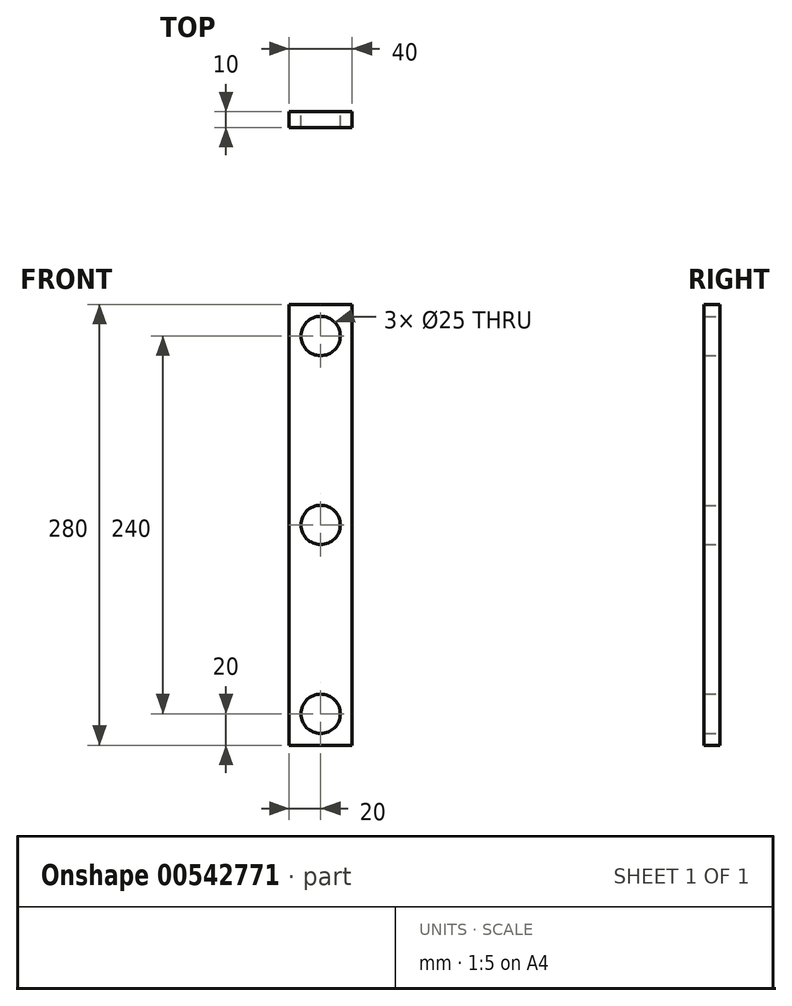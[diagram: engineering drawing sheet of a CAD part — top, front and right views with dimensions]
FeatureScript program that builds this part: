
annotation { "Feature Type Name" : "Feature", "Feature Type Description" : "" }
export const myFeature = defineFeature(function(context is Context, id is Id, definition is map)
    precondition{}
    {
        {
            var Q0;
            Q0=qCreatedBy(makeId("Front.planeOp"),FACE);
            var sketch = newSketch(context, id + "F0", { "sketchPlane" : qUnion([Q0])});
            skCircle(sketch, "E0", {"center": v(0, 0) * mm, "radius": 12.5 * mm});
            skCircle(sketch, "E1", {"center": v(0, 120) * mm, "radius": 12.5 * mm});
            skCircle(sketch, "E2", {"center": v(0, -120) * mm, "radius": 12.5 * mm});
            skLineSegment(sketch, "E3.bottom", {"start": v(-20, 140) * mm, "end": v(20, 140) * mm});
            skLineSegment(sketch, "E3.top", {"start": v(-20, -140) * mm, "end": v(20, -140) * mm});
            skLineSegment(sketch, "E3.left", {"start": v(-20, 140) * mm, "end": v(-20, -140) * mm});
            skLineSegment(sketch, "E3.right", {"start": v(20, 140) * mm, "end": v(20, -140) * mm});
            skSolve(sketch);
        }
        {
            var Q0;
            Q0=qSketchRegion(id+"F0",true);
            extrude(context, id + "F1", {"entities" : qUnion([Q0]), "endBound" : BoundingType.SYMMETRIC, "depth" : 10 * mm, "offsetDistance" : 25 * mm});
        }
    });
